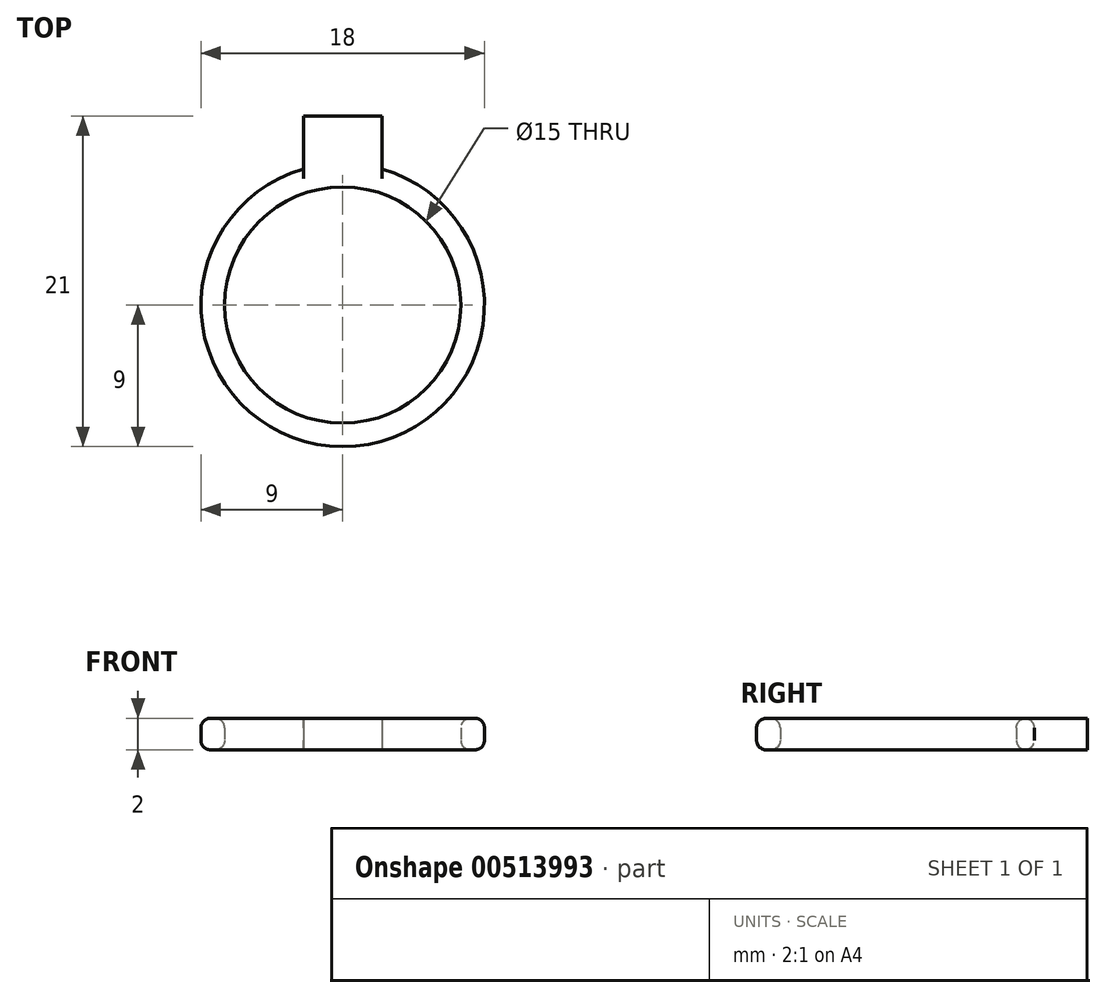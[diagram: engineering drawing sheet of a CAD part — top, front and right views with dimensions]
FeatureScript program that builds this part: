
annotation { "Feature Type Name" : "Feature", "Feature Type Description" : "" }
export const myFeature = defineFeature(function(context is Context, id is Id, definition is map)
    precondition{}
    {
        {
            var Q0;
            Q0=qCreatedBy(makeId("Top.planeOp"),FACE);
            var sketch = newSketch(context, id + "F0", { "sketchPlane" : qUnion([Q0])});
            skCircle(sketch, "E0", {"center": v(0, 0) * mm, "radius": 7.5 * mm});
            skCircle(sketch, "E1", {"center": v(0, 0) * mm, "radius": 9 * mm});
            skLineSegment(sketch, "E2.bottom", {"start": v(-2.5, 12) * mm, "end": v(2.5, 12) * mm});
            skLineSegment(sketch, "E2.top", {"start": v(-2.5, 2) * mm, "end": v(2.5, 2) * mm});
            skLineSegment(sketch, "E2.left", {"start": v(-2.5, 12) * mm, "end": v(-2.5, 2) * mm});
            skLineSegment(sketch, "E2.right", {"start": v(2.5, 12) * mm, "end": v(2.5, 2) * mm});
            skSolve(sketch);
        }
        {
            var Q0;
            {var subQ0=sQuery(id+"F0.wireOp",EDGE,"8ezKPfSu-AAIs-uz7N-KlWI-Y2M50xcObxZu.left");var subQ1=sQuery(id+"F0.wireOp",EDGE,"E0");var subQ2=makeQuery(id+"F0.imprint","INTERSECT",VERTEX,{"derivedFrom":[subQ1,subQ0]});Q0=makeQuery(id+"F0.imprint","IMPRINT",FACE,{"disambiguationData":[TD([[makeQuery(id+"F0.imprint","IMPRINT",EDGE,{"disambiguationData":[TD([[subQ2,-1.0]])],"derivedFrom":subQ1}),-1.0]])]});}
            var Q1;
            {var subQ0=sQuery(id+"F0.wireOp",EDGE,"8ezKPfSu-AAIs-uz7N-KlWI-Y2M50xcObxZu.left");var subQ1=sQuery(id+"F0.wireOp",EDGE,"E0");var subQ2=makeQuery(id+"F0.imprint","INTERSECT",VERTEX,{"derivedFrom":[subQ1,subQ0]});Q1=makeQuery(id+"F0.imprint","IMPRINT",FACE,{"disambiguationData":[TD([[makeQuery(id+"F0.imprint","IMPRINT",EDGE,{"disambiguationData":[TD([[subQ2,1.0]])],"derivedFrom":subQ1}),-1.0]])]});}
            var Q2;
            {var subQ5=sQuery(id+"F0.wireOp",EDGE,"8ezKPfSu-AAIs-uz7N-KlWI-Y2M50xcObxZu.top");Q2=makeQuery(id+"F0.imprint","IMPRINT",FACE,{"disambiguationData":[TD([[makeQuery(id+"F0.imprint","IMPRINT",EDGE,{"derivedFrom":subQ5}),-1.0]])]});}
            var Q3;
            {var subQ5=sQuery(id+"F0.wireOp",EDGE,"E2.bottom");Q3=makeQuery(id+"F0.imprint","IMPRINT",FACE,{"disambiguationData":[TD([[makeQuery(id+"F0.imprint","IMPRINT",EDGE,{"derivedFrom":subQ5}),-1.0]])]});}
            extrude(context, id + "F1", {"entities" : qUnion([Q0, Q1, Q2, Q3]), "depth" : 2 * mm});
        }
        {
            var Q0;
            Q0=makeQuery(id+"F1.opExtrude","CAP_EDGE",EDGE,{"disambiguationData":[OSD([sQuery(id+"F0.wireOp",EDGE,"E1")])],"isStart":true});
            var Q1;
            Q1=makeQuery(id+"F1.opExtrude","CAP_EDGE",EDGE,{"disambiguationData":[OSD([sQuery(id+"F0.wireOp",EDGE,"E1")])],"isStart":false});
            var Q2;
            Q2=makeQuery(id+"F1.opExtrude","CAP_EDGE",EDGE,{"disambiguationData":[OSD([sQuery(id+"F0.wireOp",EDGE,"E0")])],"isStart":false});
            var Q3;
            Q3=makeQuery(id+"F1.opExtrude","CAP_EDGE",EDGE,{"disambiguationData":[OSD([sQuery(id+"F0.wireOp",EDGE,"E0")])],"isStart":true});
            fillet(context, id + "F2", {"entities" : qUnion([Q0, Q1, Q2, Q3]), "radius" : 0.6 * mm, "tangentPropagation" : true, "allowEdgeOverflow" : false});
        }
    });
